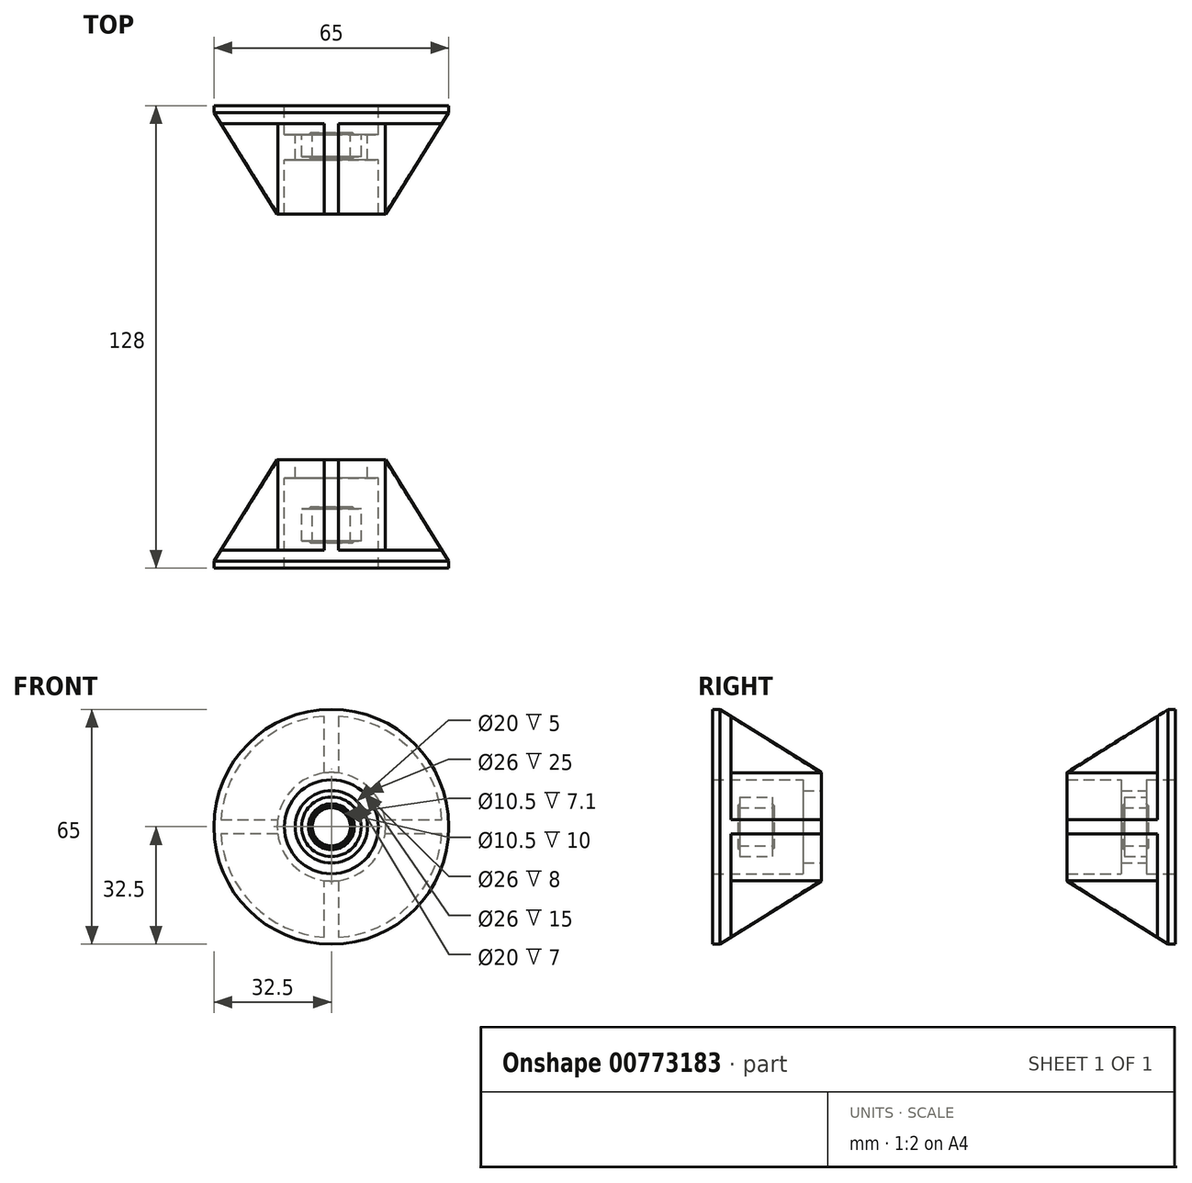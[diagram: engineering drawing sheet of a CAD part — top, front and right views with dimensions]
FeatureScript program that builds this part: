
annotation { "Feature Type Name" : "Feature", "Feature Type Description" : "" }
export const myFeature = defineFeature(function(context is Context, id is Id, definition is map)
    precondition{}
    {
        {
            var Q0;
            Q0=qCreatedBy(makeId("Right.planeOp"),FACE);
            var sketch = newSketch(context, id + "F0", { "sketchPlane" : qUnion([Q0])});
            skLineSegment(sketch, "E0", {"start": v(0, 13) * mm, "end": v(-8, 13) * mm});
            skLineSegment(sketch, "E1", {"start": v(-8, 13) * mm, "end": v(-8, 10) * mm});
            skLineSegment(sketch, "E2", {"start": v(-8, 10) * mm, "end": v(-15, 10) * mm});
            skLineSegment(sketch, "E3", {"start": v(0, 32.5) * mm, "end": v(0, 32.5) * mm});
            skLineSegment(sketch, "E4", {"start": v(0, 32.5) * mm, "end": v(0, 13) * mm});
            skLineSegment(sketch, "E5", {"start": v(-2, 32.5) * mm, "end": v(0, 32.5) * mm});
            skLineSegment(sketch, "E6", {"start": v(-15, 10) * mm, "end": v(-15, 13) * mm});
            skLineSegment(sketch, "E7", {"start": v(-15, 13) * mm, "end": v(-30, 13) * mm});
            skLineSegment(sketch, "E8", {"start": v(-30, 13) * mm, "end": v(-30, 15) * mm});
            skLineSegment(sketch, "E9", {"start": v(-30, 15) * mm, "end": v(-2, 32.5) * mm});
            skLineSegment(sketch, "E10.MirrorCS", {"start": v(-2, -32.5) * mm, "end": v(0, -32.5) * mm});
            skLineSegment(sketch, "E11.MirrorCS", {"start": v(-30, -13) * mm, "end": v(-30, -15) * mm});
            skLineSegment(sketch, "E12.MirrorCS", {"start": v(0, -32.5) * mm, "end": v(0, -32.5) * mm});
            skLineSegment(sketch, "E13.MirrorCS", {"start": v(0, -13) * mm, "end": v(-8, -13) * mm});
            skLineSegment(sketch, "E14.MirrorCS", {"start": v(-8, -13) * mm, "end": v(-8, -10) * mm});
            skLineSegment(sketch, "E15.MirrorCS", {"start": v(-15, -10) * mm, "end": v(-15, -13) * mm});
            skLineSegment(sketch, "E16.MirrorCS", {"start": v(-30, -15) * mm, "end": v(-2, -32.5) * mm});
            skLineSegment(sketch, "E17.MirrorCS", {"start": v(-15, -13) * mm, "end": v(-30, -13) * mm});
            skLineSegment(sketch, "E18.MirrorCS", {"start": v(0, -32.5) * mm, "end": v(0, -13) * mm});
            skLineSegment(sketch, "E19.MirrorCS", {"start": v(-8, -10) * mm, "end": v(-15, -10) * mm});
            skLineSegment(sketch, "E20", {"start": v(0, 0) * mm, "end": v(-55.7, 0) * mm, "construction": true});
            skLineSegment(sketch, "E21", {"start": v(-98, -10) * mm, "end": v(-103, -10) * mm});
            skLineSegment(sketch, "E22", {"start": v(-103, -10) * mm, "end": v(-103, -13) * mm});
            skLineSegment(sketch, "E23", {"start": v(-103, -13) * mm, "end": v(-128, -13) * mm});
            skLineSegment(sketch, "E24", {"start": v(-128, -13) * mm, "end": v(-128, -32.5) * mm});
            skLineSegment(sketch, "E25", {"start": v(-30, -15) * mm, "end": v(0, -15) * mm, "construction": true});
            skLineSegment(sketch, "E26", {"start": v(-128, -32.5) * mm, "end": v(-126, -32.5) * mm});
            skLineSegment(sketch, "E27", {"start": v(-15.42, -15) * mm, "end": v(-15.42, -10) * mm, "construction": true});
            skLineSegment(sketch, "E28", {"start": v(-98, -10) * mm, "end": v(-98, -15) * mm});
            skLineSegment(sketch, "E29", {"start": v(-98, -15) * mm, "end": v(-126, -32.5) * mm});
            skLineSegment(sketch, "E30", {"start": v(-8, 8.25) * mm, "end": v(-14.1, 8.25) * mm});
            skLineSegment(sketch, "E31", {"start": v(-14.1, 8.25) * mm, "end": v(-14.1, 5.25) * mm});
            skLineSegment(sketch, "E32", {"start": v(-14.1, 5.25) * mm, "end": v(-8, 5.25) * mm});
            skLineSegment(sketch, "E33", {"start": v(-8, 5.25) * mm, "end": v(-8, 8.25) * mm});
            skLineSegment(sketch, "E34.MirrorCS", {"start": v(-8, -5.25) * mm, "end": v(-8, -8.25) * mm});
            skLineSegment(sketch, "E35.MirrorCS", {"start": v(-14.1, -5.25) * mm, "end": v(-8, -5.25) * mm});
            skLineSegment(sketch, "E36.MirrorCS", {"start": v(-14.1, -8.25) * mm, "end": v(-14.1, -5.25) * mm});
            skLineSegment(sketch, "E37.MirrorCS", {"start": v(-8, -8.25) * mm, "end": v(-14.1, -8.25) * mm});
            skLineSegment(sketch, "E38.bottom", {"start": v(-111.5, -8.25) * mm, "end": v(-120.5, -8.25) * mm});
            skLineSegment(sketch, "E38.right", {"start": v(-120.5, -8.25) * mm, "end": v(-120.5, -6.35) * mm});
            skLineSegment(sketch, "E39", {"start": v(-98, -15) * mm, "end": v(-128, -15) * mm, "construction": true});
            skLineSegment(sketch, "E40", {"start": v(-14, -25) * mm, "end": v(-114, -25) * mm});
            skLineSegment(sketch, "E41", {"start": v(-14.1, 5.25) * mm, "end": v(-14.6, 5.25) * mm});
            skLineSegment(sketch, "E42", {"start": v(-14.6, 5.25) * mm, "end": v(-14.6, 5.85) * mm});
            skLineSegment(sketch, "E43", {"start": v(-14.6, 5.85) * mm, "end": v(-14.1, 6.35) * mm});
            skLineSegment(sketch, "E44", {"start": v(-11.05, 8.25) * mm, "end": v(-11.05, 5.25) * mm, "construction": true});
            skLineSegment(sketch, "E45.MirrorCS", {"start": v(-7.5, 5.85) * mm, "end": v(-8, 6.35) * mm});
            skLineSegment(sketch, "E46.MirrorCS", {"start": v(-7.5, 5.25) * mm, "end": v(-7.5, 5.85) * mm});
            skLineSegment(sketch, "E47.MirrorCS", {"start": v(-8, 5.25) * mm, "end": v(-7.5, 5.25) * mm});
            skLineSegment(sketch, "E48.MirrorCS", {"start": v(-121, -5.25) * mm, "end": v(-121, -5.85) * mm});
            skLineSegment(sketch, "E49.MirrorCS", {"start": v(-121, -5.85) * mm, "end": v(-120.5, -6.35) * mm});
            skLineSegment(sketch, "E50", {"start": v(-121, -5.25) * mm, "end": v(-111, -5.25) * mm});
            skLineSegment(sketch, "E51", {"start": v(-116, -5.25) * mm, "end": v(-116, -8.25) * mm, "construction": true});
            skLineSegment(sketch, "E52.MirrorCS", {"start": v(-111.5, -8.25) * mm, "end": v(-111.5, -6.35) * mm});
            skLineSegment(sketch, "E53.MirrorCS", {"start": v(-111, -5.85) * mm, "end": v(-111.5, -6.35) * mm});
            skLineSegment(sketch, "E54.MirrorCS", {"start": v(-111, -5.25) * mm, "end": v(-111, -5.85) * mm});
            skSolve(sketch);
        }
        {
            var Q0;
            Q0=makeQuery(id+"F0.imprint","IMPRINT",FACE,{"disambiguationData":[TD([[makeQuery(id+"F0.imprint","IMPRINT",EDGE,{"derivedFrom":sQuery(id+"F0.wireOp",EDGE,"E0")}),-1.0]])]});
            var Q1;
            Q1=makeQuery(id+"F0.imprint","IMPRINT",FACE,{"disambiguationData":[TD([[makeQuery(id+"F0.imprint","IMPRINT",EDGE,{"derivedFrom":sQuery(id+"F0.wireOp",EDGE,"E30")}),1.0]])]});
            var Q2;
            {var subQ0=sQuery(id+"F0.wireOp",EDGE,"E41");Q2=makeQuery(id+"F0.imprint","IMPRINT",FACE,{"disambiguationData":[TD([[makeQuery(id+"F0.imprint","IMPRINT",EDGE,{"derivedFrom":subQ0}),-1.0]])]});}
            var Q3;
            {var subQ2=sQuery(id+"F0.wireOp",EDGE,"E45.MirrorCS");Q3=makeQuery(id+"F0.imprint","IMPRINT",FACE,{"disambiguationData":[TD([[makeQuery(id+"F0.imprint","IMPRINT",EDGE,{"derivedFrom":subQ2}),1.0]])]});}
            var Q4;
            Q4=sQuery(id+"F0.wireOp",EDGE,"E20");
            revolve(context, id + "F1", {"surfaceOperationType" : NewSurfaceOperationType.NEW, "entities" : qUnion([Q0, Q1, Q2, Q3]), "axis" : qUnion([Q4]), "revolveType" : RevolveType.FULL});
        }
        {
            var Q0;
            Q0=makeQuery(id+"F1.opRevolve","SWEPT_FACE",FACE,{"disambiguationData":[OSD([sQuery(id+"F0.wireOp",EDGE,"E8")])]});
            var sketch = newSketch(context, id + "F2", { "sketchPlane" : qUnion([Q0])});
            skArc(sketch, "E55.0", {"start": v(2, 14.87) * mm, "mid": v(10.6, 10.6) * mm, "end": v(14.87, 2) * mm});
            skLineSegment(sketch, "E56", {"start": v(2, 14.87) * mm, "end": v(2, 40.87) * mm});
            skLineSegment(sketch, "E57", {"start": v(2, 40.87) * mm, "end": v(40.87, 40.87) * mm});
            skLineSegment(sketch, "E58", {"start": v(40.87, 40.87) * mm, "end": v(40.87, 2) * mm});
            skLineSegment(sketch, "E59", {"start": v(40.87, 2) * mm, "end": v(14.87, 2) * mm});
            skArc(sketch, "E60.1.0", {"start": v(-14.87, 2) * mm, "mid": v(-10.6, 10.6) * mm, "end": v(-2, 14.87) * mm});
            skLineSegment(sketch, "E60.1.1", {"start": v(-14.87, 2) * mm, "end": v(-40.87, 2) * mm});
            skLineSegment(sketch, "E60.1.2", {"start": v(-40.87, 2) * mm, "end": v(-40.87, 40.87) * mm});
            skLineSegment(sketch, "E60.1.3", {"start": v(-40.87, 40.87) * mm, "end": v(-2, 40.87) * mm});
            skLineSegment(sketch, "E60.1.4", {"start": v(-2, 40.87) * mm, "end": v(-2, 14.87) * mm});
            skArc(sketch, "E60.2.0", {"start": v(-2, -14.87) * mm, "mid": v(-10.6, -10.6) * mm, "end": v(-14.87, -2) * mm});
            skLineSegment(sketch, "E60.2.1", {"start": v(-2, -14.87) * mm, "end": v(-2, -40.87) * mm});
            skLineSegment(sketch, "E60.2.2", {"start": v(-2, -40.87) * mm, "end": v(-40.87, -40.87) * mm});
            skLineSegment(sketch, "E60.2.3", {"start": v(-40.87, -40.87) * mm, "end": v(-40.87, -2) * mm});
            skLineSegment(sketch, "E60.2.4", {"start": v(-40.87, -2) * mm, "end": v(-14.87, -2) * mm});
            skArc(sketch, "E60.3.0", {"start": v(14.87, -2) * mm, "mid": v(10.6, -10.6) * mm, "end": v(2, -14.87) * mm});
            skLineSegment(sketch, "E60.3.1", {"start": v(14.87, -2) * mm, "end": v(40.87, -2) * mm});
            skLineSegment(sketch, "E60.3.2", {"start": v(40.87, -2) * mm, "end": v(40.87, -40.87) * mm});
            skLineSegment(sketch, "E60.3.3", {"start": v(40.87, -40.87) * mm, "end": v(2, -40.87) * mm});
            skLineSegment(sketch, "E60.3.4", {"start": v(2, -40.87) * mm, "end": v(2, -14.87) * mm});
            skLineSegment(sketch, "E60.anchor1", {"start": v(0, 0) * mm, "end": v(14.87, 2) * mm, "construction": true});
            skLineSegment(sketch, "E60.anchor2", {"start": v(0, 0) * mm, "end": v(2, -14.87) * mm, "construction": true});
            skSolve(sketch);
        }
        {
            var Q0;
            Q0 = qSketchRegion(id + "F2", true);
            extrude(context, id + "F3", {"entities" : qUnion([Q0]), "operationType" : NewBodyOperationType.REMOVE, "oppositeDirection" : true, "depth" : 25 * mm, "offsetDistance" : 25 * mm});
        }
        {
            var Q0;
            Q0=makeQuery(id+"F0.imprint","IMPRINT",FACE,{"disambiguationData":[TD([[makeQuery(id+"F0.imprint","IMPRINT",EDGE,{"derivedFrom":sQuery(id+"F0.wireOp",EDGE,"E21")}),1.0]])]});
            var Q1;
            Q1=makeQuery(id+"F0.imprint","IMPRINT",FACE,{"disambiguationData":[TD([[makeQuery(id+"F0.imprint","IMPRINT",EDGE,{"derivedFrom":sQuery(id+"F0.wireOp",EDGE,"E38.bottom")}),-1.0]])]});
            var Q2;
            {var subQ0=sQuery(id+"F0.wireOp",EDGE,"d348c799-7614-4689-8eaa-a9564630b156");Q2=makeQuery(id+"F0.imprint","IMPRINT",FACE,{"disambiguationData":[TD([[makeQuery(id+"F0.imprint","IMPRINT",EDGE,{"derivedFrom":subQ0}),-1.0]])]});}
            var Q3;
            {var subQ2=sQuery(id+"F0.wireOp",EDGE,"e9968ce5-df91-4282-88b8-af8914356a3b0.MirrorCS");Q3=makeQuery(id+"F0.imprint","IMPRINT",FACE,{"disambiguationData":[TD([[makeQuery(id+"F0.imprint","IMPRINT",EDGE,{"derivedFrom":subQ2}),1.0]])]});}
            var Q4;
            Q4=makeQuery(id+"F0.imprint","IMPRINT",FACE,{"disambiguationData":[TD([[makeQuery(id+"F0.imprint","IMPRINT",EDGE,{"derivedFrom":sQuery(id+"F0.wireOp",EDGE,"E48.MirrorCS")}),1.0]])]});
            var Q5;
            Q5=makeQuery(id+"F0.imprint","IMPRINT",FACE,{"disambiguationData":[TD([[makeQuery(id+"F0.imprint","IMPRINT",EDGE,{"derivedFrom":sQuery(id+"F0.wireOp",EDGE,"12ca7649-3b13-406e-a90d-596a61859a5c0.MirrorCS")}),-1.0]])]});
            var Q6;
            Q6=sQuery(id+"F0.wireOp",EDGE,"E20");
            revolve(context, id + "F4", {"surfaceOperationType" : NewSurfaceOperationType.NEW, "entities" : qUnion([Q0, Q1, Q2, Q3, Q4, Q5]), "axis" : qUnion([Q6]), "revolveType" : RevolveType.FULL});
        }
        {
            var Q0;
            Q0=makeQuery(id+"F4.opRevolve","SWEPT_FACE",FACE,{"disambiguationData":[OSD([sQuery(id+"F0.wireOp",EDGE,"E28")])]});
            var sketch = newSketch(context, id + "F5", { "sketchPlane" : qUnion([Q0])});
            skArc(sketch, "E61.0", {"start": v(2, 14.87) * mm, "mid": v(10.6, 10.6) * mm, "end": v(14.87, 2) * mm});
            skLineSegment(sketch, "E62", {"start": v(2, 14.87) * mm, "end": v(2, 41.71) * mm});
            skLineSegment(sketch, "E63", {"start": v(2, 41.71) * mm, "end": v(41.71, 41.71) * mm});
            skLineSegment(sketch, "E64", {"start": v(41.71, 41.71) * mm, "end": v(41.71, 2) * mm});
            skLineSegment(sketch, "E65", {"start": v(41.71, 2) * mm, "end": v(14.87, 2) * mm});
            skArc(sketch, "E66.1.0", {"start": v(-14.87, 2) * mm, "mid": v(-10.6, 10.6) * mm, "end": v(-2, 14.87) * mm});
            skLineSegment(sketch, "E66.1.1", {"start": v(-14.87, 2) * mm, "end": v(-41.71, 2) * mm});
            skLineSegment(sketch, "E66.1.2", {"start": v(-41.71, 2) * mm, "end": v(-41.71, 41.71) * mm});
            skLineSegment(sketch, "E66.1.3", {"start": v(-41.71, 41.71) * mm, "end": v(-2, 41.71) * mm});
            skLineSegment(sketch, "E66.1.4", {"start": v(-2, 41.71) * mm, "end": v(-2, 14.87) * mm});
            skArc(sketch, "E66.2.0", {"start": v(-2, -14.87) * mm, "mid": v(-10.6, -10.6) * mm, "end": v(-14.87, -2) * mm});
            skLineSegment(sketch, "E66.2.1", {"start": v(-2, -14.87) * mm, "end": v(-2, -41.71) * mm});
            skLineSegment(sketch, "E66.2.2", {"start": v(-2, -41.71) * mm, "end": v(-41.71, -41.71) * mm});
            skLineSegment(sketch, "E66.2.3", {"start": v(-41.71, -41.71) * mm, "end": v(-41.71, -2) * mm});
            skLineSegment(sketch, "E66.2.4", {"start": v(-41.71, -2) * mm, "end": v(-14.87, -2) * mm});
            skArc(sketch, "E66.3.0", {"start": v(14.87, -2) * mm, "mid": v(10.6, -10.6) * mm, "end": v(2, -14.87) * mm});
            skLineSegment(sketch, "E66.3.1", {"start": v(14.87, -2) * mm, "end": v(41.71, -2) * mm});
            skLineSegment(sketch, "E66.3.2", {"start": v(41.71, -2) * mm, "end": v(41.71, -41.71) * mm});
            skLineSegment(sketch, "E66.3.3", {"start": v(41.71, -41.71) * mm, "end": v(2, -41.71) * mm});
            skLineSegment(sketch, "E66.3.4", {"start": v(2, -41.71) * mm, "end": v(2, -14.87) * mm});
            skLineSegment(sketch, "E66.anchor1", {"start": v(0, 0) * mm, "end": v(14.87, 2) * mm, "construction": true});
            skLineSegment(sketch, "E66.anchor2", {"start": v(0, 0) * mm, "end": v(2, -14.87) * mm, "construction": true});
            skSolve(sketch);
        }
        {
            var Q0;
            Q0=makeQuery(id+"F5.imprint","IMPRINT",FACE,{"disambiguationData":[TD([[makeQuery(id+"F5.imprint","IMPRINT",EDGE,{"derivedFrom":sQuery(id+"F5.wireOp",EDGE,"E66.2.0")}),-1.0]])]});
            var Q1;
            Q1=makeQuery(id+"F5.imprint","IMPRINT",FACE,{"disambiguationData":[TD([[makeQuery(id+"F5.imprint","IMPRINT",EDGE,{"derivedFrom":sQuery(id+"F5.wireOp",EDGE,"E66.3.0")}),-1.0]])]});
            var Q2;
            Q2=makeQuery(id+"F5.imprint","IMPRINT",FACE,{"disambiguationData":[TD([[makeQuery(id+"F5.imprint","IMPRINT",EDGE,{"derivedFrom":sQuery(id+"F5.wireOp",EDGE,"E61.0")}),-1.0]])]});
            var Q3;
            Q3=makeQuery(id+"F5.imprint","IMPRINT",FACE,{"disambiguationData":[TD([[makeQuery(id+"F5.imprint","IMPRINT",EDGE,{"derivedFrom":sQuery(id+"F5.wireOp",EDGE,"E66.1.0")}),-1.0]])]});
            var Q4;
            Q4 = qConstructionFilter(qBodyType(qCreatedBy(id + "F5" ,EDGE), BodyType.WIRE), ConstructionObject.NO);
            extrude(context, id + "F6", {"entities" : qUnion([Q0, Q1, Q2, Q3]), "operationType" : NewBodyOperationType.REMOVE, "surfaceEntities" : qUnion([Q4]), "oppositeDirection" : true, "depth" : 25 * mm, "offsetDistance" : 25 * mm});
        }
    });
